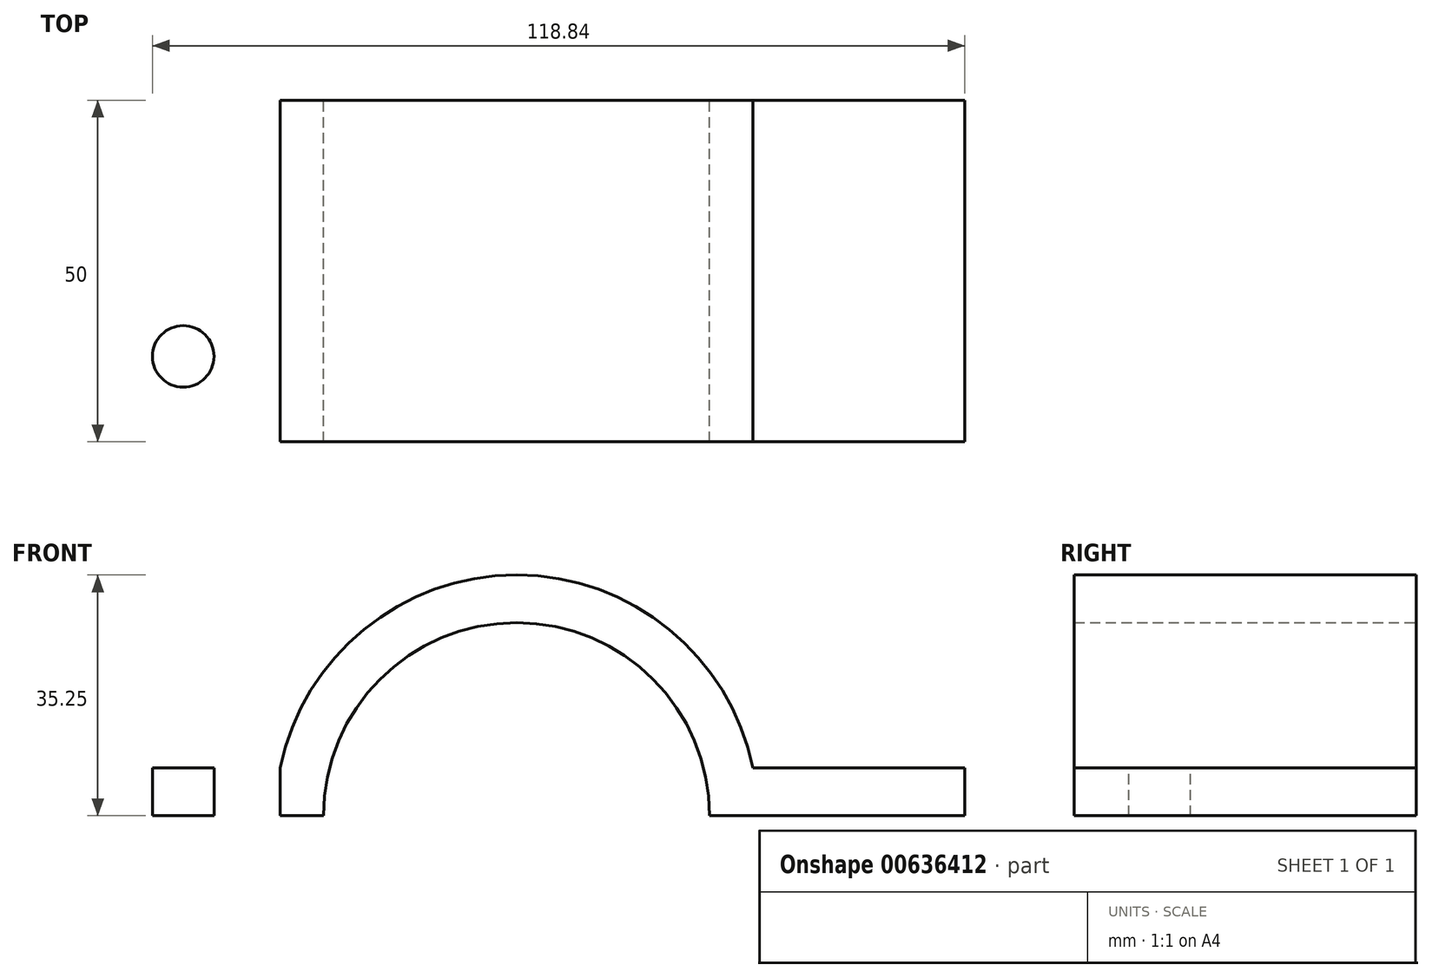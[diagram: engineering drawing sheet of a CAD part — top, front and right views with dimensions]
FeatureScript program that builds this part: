
annotation { "Feature Type Name" : "Feature", "Feature Type Description" : "" }
export const myFeature = defineFeature(function(context is Context, id is Id, definition is map)
    precondition{}
    {
        {
            var Q0;
            Q0=qCreatedBy(makeId("Front.planeOp"),FACE);
            var sketch = newSketch(context, id + "F0", { "sketchPlane" : qUnion([Q0])});
            skArc(sketch, "E0", {"start": v(28.25, 0) * mm, "mid": v(0, 28.25) * mm, "end": v(-28.25, 0) * mm});
            skLineSegment(sketch, "E1", {"start": v(28.25, 0) * mm, "end": v(65.58, 0) * mm});
            skLineSegment(sketch, "E2", {"start": v(65.58, 0) * mm, "end": v(28.25, 0) * mm});
            skLineSegment(sketch, "E3", {"start": v(-62.96, 0) * mm, "end": v(-28.25, 0) * mm});
            skLineSegment(sketch, "E4.0", {"start": v(-62.96, 7) * mm, "end": v(-34.55, 7) * mm});
            skArc(sketch, "E4.1", {"start": v(34.55, 7) * mm, "mid": v(0, 35.25) * mm, "end": v(-34.55, 7) * mm});
            skLineSegment(sketch, "E4.2", {"start": v(65.58, 7) * mm, "end": v(34.55, 7) * mm});
            skLineSegment(sketch, "E5", {"start": v(-62.96, 7) * mm, "end": v(-62.96, 0) * mm});
            skLineSegment(sketch, "E6", {"start": v(65.58, 7) * mm, "end": v(65.58, 0) * mm});
            skSolve(sketch);
        }
        {
            var Q0;
            Q0=makeQuery(id+"F0.imprint","IMPRINT",FACE,{"disambiguationData":[TD([[makeQuery(id+"F0.imprint","IMPRINT",EDGE,{"derivedFrom":sQuery(id+"F0.wireOp",EDGE,"E0")}),-1.0]])]});
            extrude(context, id + "F1", {"entities" : qUnion([Q0]), "endBound" : BoundingType.SYMMETRIC, "depth" : 50 * mm, "offsetDistance" : 25 * mm});
        }
        {
            var Q0;
            Q0=makeQuery(id+"F1.opExtrude","SWEPT_FACE",FACE,{"disambiguationData":[OSD([sQuery(id+"F0.wireOp",EDGE,"E4.0")])]});
            var sketch = newSketch(context, id + "F2", { "sketchPlane" : qUnion([Q0])});
            skLineSegment(sketch, "E7", {"start": v(-62.96, 0) * mm, "end": v(-34.55, 0) * mm, "construction": true});
            skLineSegment(sketch, "E8", {"start": v(-48.76, 0) * mm, "end": v(-48.76, 25) * mm, "construction": true});
            skPoint(sketch, "E9", {"position": v(-48.76, 12.5) * mm});
            skCircle(sketch, "E10", {"center": v(-48.76, 12.5) * mm, "radius": 4.5 * mm});
            skCircle(sketch, "E11.MirrorC", {"center": v(-48.76, -12.5) * mm, "radius": 4.5 * mm});
            skSolve(sketch);
        }
        {
            var Q0;
            Q0=makeQuery(id+"F2.imprint","IMPRINT",FACE,{"disambiguationData":[TD([[makeQuery(id+"F2.imprint","IMPRINT",EDGE,{"derivedFrom":sQuery(id+"F2.wireOp",EDGE,"E11.MirrorC")}),-1.0]])]});
            var Q1;
            Q1=makeQuery(id+"F2.imprint","IMPRINT",FACE,{"disambiguationData":[TD([[makeQuery(id+"F2.imprint","IMPRINT",EDGE,{"derivedFrom":sQuery(id+"F2.wireOp",EDGE,"E10")}),1.0]])]});
            var Q2;
            Q2=sQuery(id+"F2.wireOp",EDGE,"E10");
            var Q3;
            Q3=sQuery(id+"F2.wireOp",EDGE,"E11.MirrorC");
            extrude(context, id + "F3", {"entities" : qUnion([Q0, Q1]), "operationType" : NewBodyOperationType.REMOVE, "surfaceEntities" : qUnion([Q2, Q3]), "endBound" : BoundingType.THROUGH_ALL, "oppositeDirection" : true, "depth" : 25 * mm, "offsetDistance" : 25 * mm});
        }
    });
